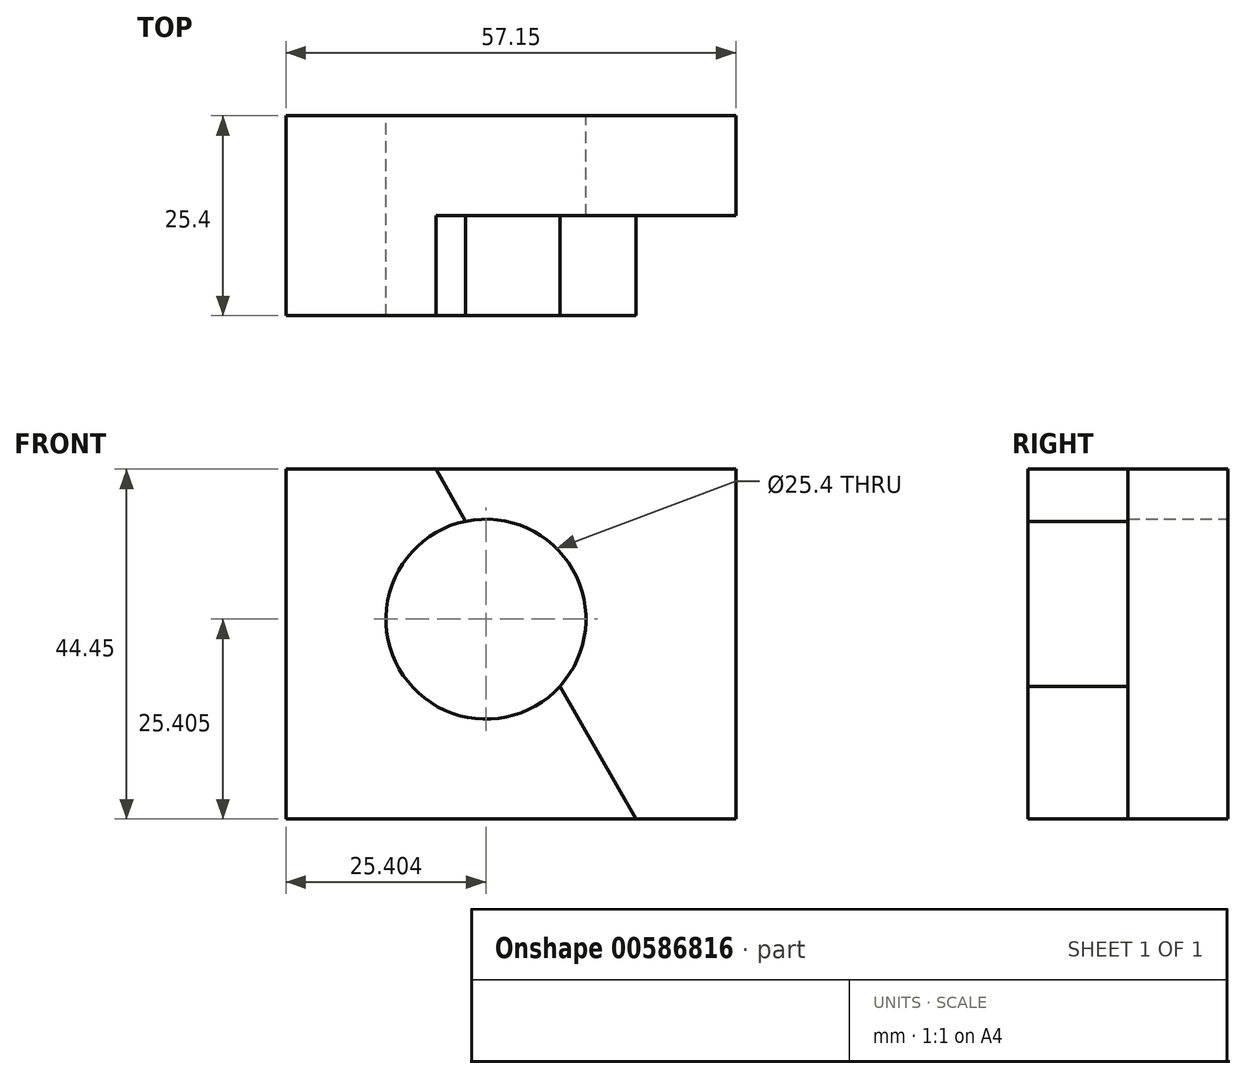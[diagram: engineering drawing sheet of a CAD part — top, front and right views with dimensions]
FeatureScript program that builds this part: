
annotation { "Feature Type Name" : "Feature", "Feature Type Description" : "" }
export const myFeature = defineFeature(function(context is Context, id is Id, definition is map)
    precondition{}
    {
        {
            var Q0;
            Q0=qCreatedBy(makeId("Front.planeOp"),FACE);
            var sketch = newSketch(context, id + "F0", { "sketchPlane" : qUnion([Q0])});
            skLineSegment(sketch, "E0", {"start": v(-64.87, 59.7) * mm, "end": v(-7.72, 59.7) * mm});
            skLineSegment(sketch, "E1", {"start": v(-7.72, 59.7) * mm, "end": v(-7.72, 15.24) * mm});
            skLineSegment(sketch, "E2", {"start": v(-7.72, 15.24) * mm, "end": v(-64.87, 15.24) * mm});
            skLineSegment(sketch, "E3", {"start": v(-64.87, 15.24) * mm, "end": v(-64.87, 59.7) * mm});
            skSolve(sketch);
        }
        {
            var Q0;
            Q0=makeQuery(id+"F0.imprint","IMPRINT",FACE,{"disambiguationData":[TD([[makeQuery(id+"F0.imprint","IMPRINT",EDGE,{"derivedFrom":sQuery(id+"F0.wireOp",EDGE,"E0")}),-1.0]])]});
            extrude(context, id + "F1", {"entities" : qUnion([Q0]), "depth" : 25.4 * mm, "offsetDistance" : 25.4 * mm});
        }
        {
            var Q0;
            Q0=makeQuery(id+"F1.opExtrude","CAP_FACE",FACE,{"disambiguationData":[OSD([sQuery(id+"F0.wireOp",EDGE,"E0"),sQuery(id+"F0.wireOp",EDGE,"E1"),sQuery(id+"F0.wireOp",EDGE,"E2"),sQuery(id+"F0.wireOp",EDGE,"E3")])],"isStart":false});
            var sketch = newSketch(context, id + "F2", { "sketchPlane" : qUnion([Q0])});
            skLineSegment(sketch, "E4", {"start": v(-45.82, 59.7) * mm, "end": v(-20.42, 15.24) * mm});
            skSolve(sketch);
        }
        {
            var Q0;
            {var subQ0=sQuery(id+"F2.wireOp",EDGE,"E4");Q0=makeQuery(id+"F2.imprint","IMPRINT",FACE,{"disambiguationData":[TD([[makeQuery(id+"F2.imprint","IMPRINT",EDGE,{"derivedFrom":subQ0}),1.0]])]});}
            extrude(context, id + "F3", {"entities" : qUnion([Q0]), "operationType" : NewBodyOperationType.REMOVE, "oppositeDirection" : true, "depth" : 12.7 * mm, "offsetDistance" : 25.4 * mm});
        }
        {
            var Q0;
            Q0=makeQuery(id+"F0.imprint","IMPRINT",FACE,{"disambiguationData":[TD([[makeQuery(id+"F0.imprint","IMPRINT",EDGE,{"derivedFrom":sQuery(id+"F0.wireOp",EDGE,"E0")}),-1.0]])]});
            var sketch = newSketch(context, id + "F4", { "sketchPlane" : qUnion([Q0])});
            skCircle(sketch, "E5", {"center": v(-39.47, 40.64) * mm, "radius": 12.7 * mm});
            skSolve(sketch);
        }
        {
            var Q0;
            Q0=makeQuery(id+"F4.imprint","IMPRINT",FACE,{"disambiguationData":[TD([[makeQuery(id+"F4.imprint","IMPRINT",EDGE,{"derivedFrom":sQuery(id+"F4.wireOp",EDGE,"E5")}),1.0]])]});
            extrude(context, id + "F5", {"entities" : qUnion([Q0]), "operationType" : NewBodyOperationType.REMOVE, "endBound" : BoundingType.THROUGH_ALL, "depth" : 25.4 * mm, "offsetDistance" : 25.4 * mm});
        }
    });
